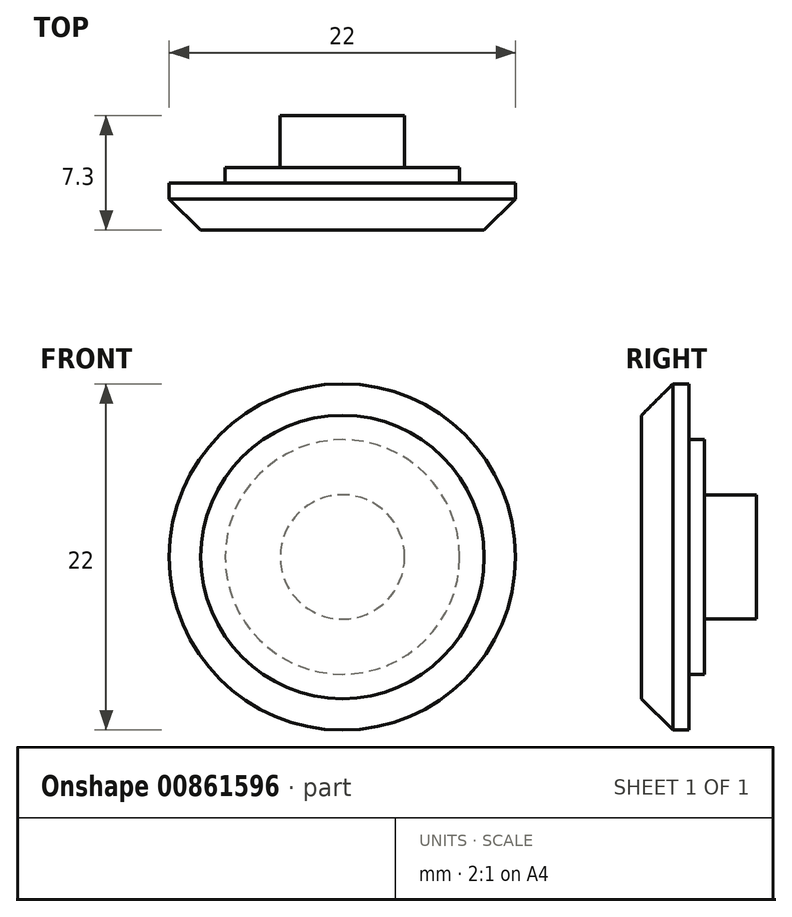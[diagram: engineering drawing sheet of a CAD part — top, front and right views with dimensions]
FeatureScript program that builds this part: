
annotation { "Feature Type Name" : "Feature", "Feature Type Description" : "" }
export const myFeature = defineFeature(function(context is Context, id is Id, definition is map)
    precondition{}
    {
        {
            var Q0;
            Q0=qCreatedBy(makeId("Top.planeOp"),FACE);
            var sketch = newSketch(context, id + "F0", { "sketchPlane" : qUnion([Q0])});
            skLineSegment(sketch, "E0", {"start": v(-11, 0) * mm, "end": v(-11, 3) * mm});
            skLineSegment(sketch, "E1", {"start": v(-11, 3) * mm, "end": v(-7.45, 3) * mm});
            skLineSegment(sketch, "E2", {"start": v(-7.45, 3) * mm, "end": v(-7.45, 4) * mm});
            skLineSegment(sketch, "E3", {"start": v(-7.45, 4) * mm, "end": v(-3.95, 4) * mm});
            skLineSegment(sketch, "E4", {"start": v(-3.95, 4) * mm, "end": v(-3.95, 7.3) * mm});
            skLineSegment(sketch, "E5", {"start": v(-3.95, 7.3) * mm, "end": v(0, 7.3) * mm});
            skLineSegment(sketch, "E6", {"start": v(0, 7.3) * mm, "end": v(0, 0) * mm});
            skLineSegment(sketch, "E7", {"start": v(0, 0) * mm, "end": v(-11, 0) * mm});
            skSolve(sketch);
        }
        {
            var Q0;
            Q0=makeQuery(id+"F0.imprint","IMPRINT",FACE,{"disambiguationData":[TD([[makeQuery(id+"F0.imprint","IMPRINT",EDGE,{"derivedFrom":sQuery(id+"F0.wireOp",EDGE,"E0")}),-1.0]])]});
            var Q1;
            Q1=sQuery(id+"F0.wireOp",EDGE,"E6");
            revolve(context, id + "F1", {"surfaceOperationType" : NewSurfaceOperationType.NEW, "entities" : qUnion([Q0]), "axis" : qUnion([Q1]), "revolveType" : RevolveType.FULL});
        }
        {
            var Q0;
            Q0=makeQuery(id+"F1.opRevolve","SWEPT_FACE",FACE,{"disambiguationData":[OSD([sQuery(id+"F0.wireOp",EDGE,"E7")])]});
            chamfer(context, id + "F2", {"entities" : qUnion([Q0]), "width" : 2 * mm, "tangentPropagation" : true});
        }
    });
